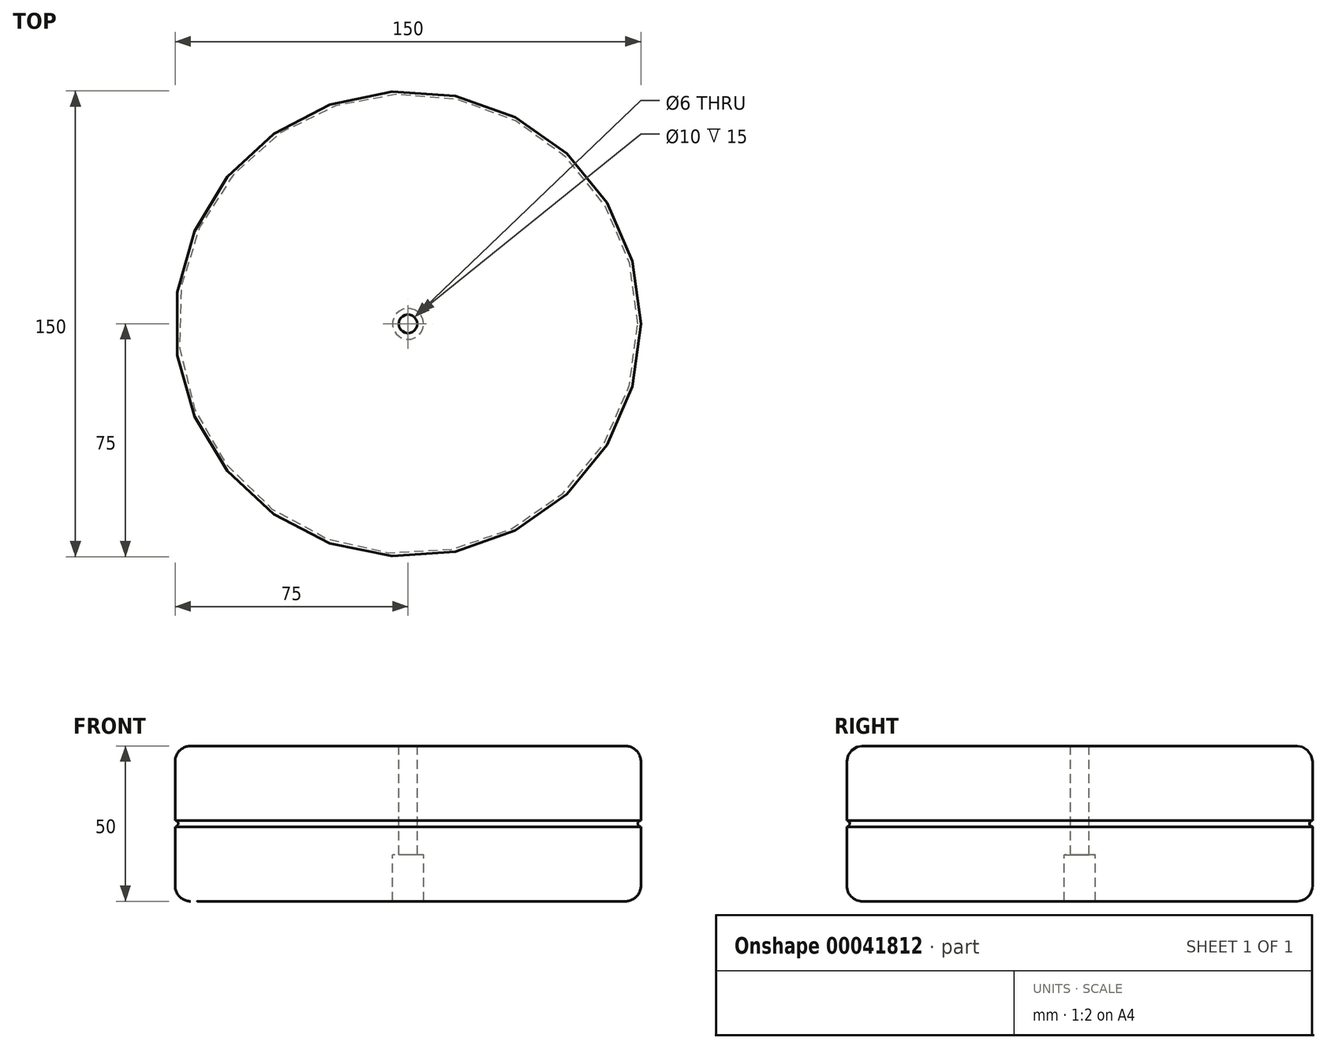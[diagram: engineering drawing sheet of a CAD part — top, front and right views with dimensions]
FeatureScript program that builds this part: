
annotation { "Feature Type Name" : "Feature", "Feature Type Description" : "" }
export const myFeature = defineFeature(function(context is Context, id is Id, definition is map)
    precondition{}
    {
        {
            var Q0;
            Q0=qCreatedBy(makeId("Front.planeOp"),FACE);
            var sketch = newSketch(context, id + "F0", { "sketchPlane" : qUnion([Q0])});
            skLineSegment(sketch, "E0.bottom", {"start": v(5, 0) * mm, "end": v(70, 0) * mm});
            skLineSegment(sketch, "E0.top", {"start": v(3, 50) * mm, "end": v(70, 50) * mm});
            skLineSegment(sketch, "E0.right", {"start": v(75, 5) * mm, "end": v(75, 24) * mm});
            skPoint(sketch, "E1.visualSharp", {"position": v(75, 50) * mm});
            skArc(sketch, "E1.filletArc", {"start": v(75, 45) * mm, "mid": v(73.54, 48.54) * mm, "end": v(70, 50) * mm});
            skPoint(sketch, "E2.visualSharp", {"position": v(75, 0) * mm});
            skArc(sketch, "E2.filletArc", {"start": v(70, 0) * mm, "mid": v(73.54, 1.46) * mm, "end": v(75, 5) * mm});
            skArc(sketch, "E3", {"start": v(75, 26) * mm, "mid": v(74, 25) * mm, "end": v(75, 24) * mm});
            skLineSegment(sketch, "E4.trimOffspring", {"start": v(75, 26) * mm, "end": v(75, 45) * mm});
            skLineSegment(sketch, "E5.top", {"start": v(3, 15) * mm, "end": v(5, 15) * mm});
            skLineSegment(sketch, "E5.right", {"start": v(3, 50) * mm, "end": v(3, 15) * mm});
            skLineSegment(sketch, "E6.right", {"start": v(5, 15) * mm, "end": v(5, 0) * mm});
            skPoint(sketch, "E7.orphan", {"position": v(0, 50) * mm});
            skPoint(sketch, "E8.orphan", {"position": v(0, 0) * mm});
            skLineSegment(sketch, "E9", {"start": v(0, 50) * mm, "end": v(0, 0) * mm});
            skSolve(sketch);
        }
        {
            var Q0;
            Q0=makeQuery(id+"F0.imprint","IMPRINT",FACE,{"disambiguationData":[TD([[makeQuery(id+"F0.imprint","IMPRINT",EDGE,{"derivedFrom":sQuery(id+"F0.wireOp",EDGE,"E0.bottom")}),1.0]])]});
            var Q1;
            Q1=sQuery(id+"F0.wireOp",EDGE,"E9");
            revolve(context, id + "F1", {"entities" : qUnion([Q0]), "axis" : qUnion([Q1]), "revolveType" : RevolveType.FULL});
        }
    });
